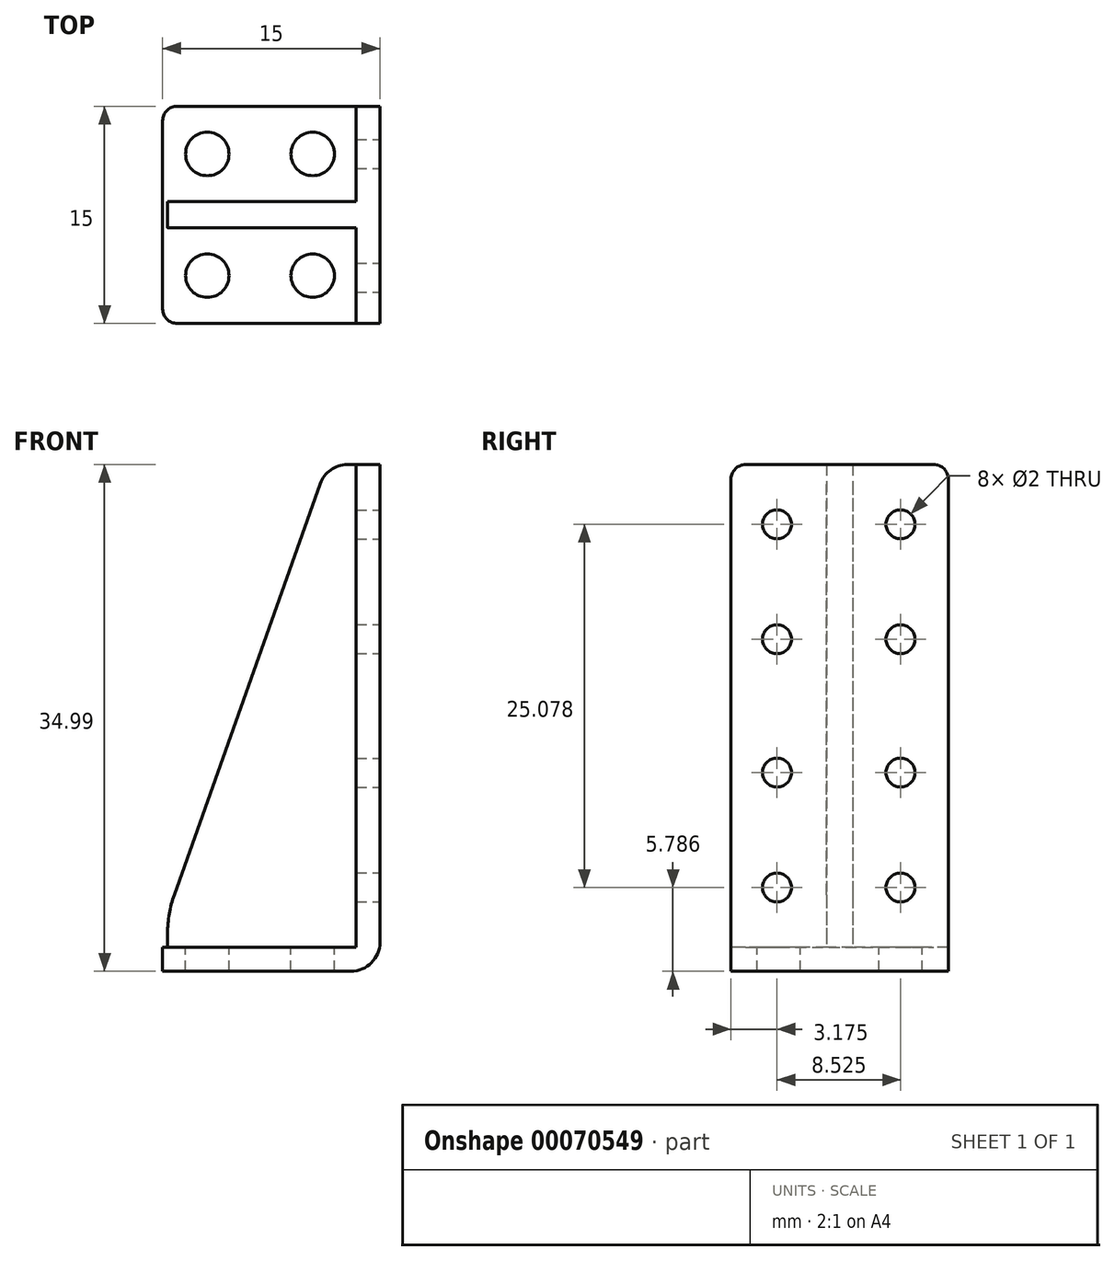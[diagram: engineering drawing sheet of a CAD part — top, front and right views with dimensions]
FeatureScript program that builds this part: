
annotation { "Feature Type Name" : "Feature", "Feature Type Description" : "" }
export const myFeature = defineFeature(function(context is Context, id is Id, definition is map)
    precondition{}
    {
        {
            var Q0;
            Q0=qCreatedBy(makeId("Top.planeOp"),FACE);
            var sketch = newSketch(context, id + "F0", { "sketchPlane" : qUnion([Q0])});
            skLineSegment(sketch, "E0.bottom", {"start": v(0, 0) * mm, "end": v(15, 0) * mm});
            skLineSegment(sketch, "E0.top", {"start": v(0, 15) * mm, "end": v(15, 15) * mm});
            skLineSegment(sketch, "E0.left", {"start": v(0, 0) * mm, "end": v(0, 15) * mm});
            skLineSegment(sketch, "E0.right", {"start": v(15, 0) * mm, "end": v(15, 15) * mm});
            skSolve(sketch);
        }
        {
            var Q0;
            Q0 = qSketchRegion(id + "F0", true);
            extrude(context, id + "F1", {"entities" : qUnion([Q0]), "depth" : 1.66 * mm});
        }
        {
            var Q0;
            Q0=makeQuery(id+"F1.opExtrude","CAP_FACE",FACE,{"disambiguationData":[OSD([sQuery(id+"F0.wireOp",EDGE,"E0.bottom"),sQuery(id+"F0.wireOp",EDGE,"E0.top"),sQuery(id+"F0.wireOp",EDGE,"E0.left"),sQuery(id+"F0.wireOp",EDGE,"E0.right")])],"isStart":false});
            var sketch = newSketch(context, id + "F2", { "sketchPlane" : qUnion([Q0])});
            skLineSegment(sketch, "E1.bottom", {"start": v(15, 15) * mm, "end": v(13.34, 15) * mm});
            skLineSegment(sketch, "E1.top", {"start": v(15, 0) * mm, "end": v(13.34, 0) * mm});
            skLineSegment(sketch, "E1.left", {"start": v(15, 15) * mm, "end": v(15, 0) * mm});
            skLineSegment(sketch, "E1.right", {"start": v(13.34, 15) * mm, "end": v(13.34, 0) * mm});
            skSolve(sketch);
        }
        {
            var Q0;
            Q0 = qSketchRegion(id + "F2", true);
            extrude(context, id + "F3", {"entities" : qUnion([Q0]), "operationType" : NewBodyOperationType.ADD, "depth" : 33.33 * mm});
        }
        {
            var Q0;
            Q0=makeQuery(id+"F3.opExtrude","SWEPT_FACE",FACE,{"disambiguationData":[OSD([sQuery(id+"F2.wireOp",EDGE,"E1.right")])]});
            var sketch = newSketch(context, id + "F4", { "sketchPlane" : qUnion([Q0])});
            skLineSegment(sketch, "E2", {"start": v(-7.5, 35) * mm, "end": v(-7.5, -12.6) * mm, "construction": true});
            skLineSegment(sketch, "E3", {"start": v(-7.5, 35) * mm, "end": v(-6.6, 35) * mm});
            skLineSegment(sketch, "E4", {"start": v(-6.6, 35) * mm, "end": v(-6.6, 1.66) * mm});
            skLineSegment(sketch, "E5", {"start": v(-6.6, 1.66) * mm, "end": v(-7.5, 1.66) * mm});
            skLineSegment(sketch, "E6.MirrorCS", {"start": v(-8.4, 35) * mm, "end": v(-8.4, 1.66) * mm});
            skLineSegment(sketch, "E7.MirrorCS", {"start": v(-8.4, 1.66) * mm, "end": v(-7.5, 1.66) * mm});
            skLineSegment(sketch, "E8.MirrorCS", {"start": v(-7.5, 35) * mm, "end": v(-8.4, 35) * mm});
            skSolve(sketch);
        }
        {
            var Q0;
            Q0 = qSketchRegion(id + "F4", true);
            extrude(context, id + "F5", {"entities" : qUnion([Q0]), "operationType" : NewBodyOperationType.ADD, "depth" : 13 * mm});
        }
        {
            var Q0;
            Q0=makeQuery(id+"F5.opExtrude","CAP_EDGE",EDGE,{"disambiguationData":[OSD([sQuery(id+"F4.wireOp",EDGE,"E3"),sQuery(id+"F4.wireOp",EDGE,"E8.MirrorCS")])],"isStart":false});
            chamfer(context, id + "F6", {"entities" : qUnion([Q0]), "chamferType" : ChamferType.TWO_OFFSETS, "width1" : 11 * mm, "oppositeDirection" : false, "width2" : 31 * mm, "tangentPropagation" : true});
        }
        {
            var Q0;
            Q0=makeQuery(id+"F1.opExtrude","SWEPT_EDGE",EDGE,{"disambiguationData":[OSD([sQuery(id+"F0.wireOp",EDGE,"E0.bottom"),sQuery(id+"F0.wireOp",EDGE,"E0.left")])]});
            var Q1;
            Q1=makeQuery(id+"F1.opExtrude","SWEPT_EDGE",EDGE,{"disambiguationData":[OSD([sQuery(id+"F0.wireOp",EDGE,"E0.top"),sQuery(id+"F0.wireOp",EDGE,"E0.left")])]});
            var Q2;
            {var subQ0=sQuery(id+"F2.wireOp",EDGE,"E1.right");var subQ1=sQuery(id+"F0.wireOp",EDGE,"E0.bottom");Q2=makeQuery(id+"F5.boolean.opBoolean","SPLIT",EDGE,{"disambiguationData":[TD([makeQuery(id+"F1.opExtrude","SWEPT_FACE",FACE,{"disambiguationData":[OSD([subQ1])]})])],"derivedFrom":makeQuery(id+"F3.opExtrude","CAP_EDGE",EDGE,{"disambiguationData":[OSD([subQ0])],"isStart":true})});}
            var Q3;
            {var subQ0=sQuery(id+"F2.wireOp",EDGE,"E1.right");var subQ1=sQuery(id+"F0.wireOp",EDGE,"E0.top");Q3=makeQuery(id+"F5.boolean.opBoolean","SPLIT",EDGE,{"disambiguationData":[TD([makeQuery(id+"F1.opExtrude","SWEPT_FACE",FACE,{"disambiguationData":[OSD([subQ1])]})])],"derivedFrom":makeQuery(id+"F3.opExtrude","CAP_EDGE",EDGE,{"disambiguationData":[OSD([subQ0])],"isStart":true})});}
            var Q4;
            Q4=makeQuery(id+"F3.opExtrude","CAP_EDGE",EDGE,{"disambiguationData":[OSD([sQuery(id+"F2.wireOp",EDGE,"E1.bottom")])],"isStart":false});
            var Q5;
            Q5=makeQuery(id+"F3.opExtrude","CAP_EDGE",EDGE,{"disambiguationData":[OSD([sQuery(id+"F2.wireOp",EDGE,"E1.top")])],"isStart":false});
            fillet(context, id + "F7", {"entities" : qUnion([Q0, Q1, Q2, Q3, Q4, Q5]), "radius" : 1 * mm, "tangentPropagation" : true, "allowEdgeOverflow" : false});
        }
        {
            var Q0;
            {var subQ0=sQuery(id+"F4.wireOp",EDGE,"E8.MirrorCS");var subQ1=sQuery(id+"F4.wireOp",EDGE,"E3");Q0=makeQuery(id+"F6.opChamfer","BLEND_EDGE",EDGE,{"blendedFrom":[makeQuery(id+"F5.opExtrude","CAP_EDGE",EDGE,{"disambiguationData":[OSD([subQ1,subQ0])],"isStart":false}),makeQuery(id+"F5.boolean.opBoolean","MERGE",FACE,{"derivedFrom":[makeQuery(id+"F3.opExtrude","CAP_FACE",FACE,{"disambiguationData":[OSD([sQuery(id+"F2.wireOp",EDGE,"E1.bottom"),sQuery(id+"F2.wireOp",EDGE,"E1.top"),sQuery(id+"F2.wireOp",EDGE,"E1.left"),sQuery(id+"F2.wireOp",EDGE,"E1.right")])],"isStart":false}),makeQuery(id+"F5.opExtrude","SWEPT_FACE",FACE,{"disambiguationData":[OSD([subQ1,subQ0])]})]})],"blendedInto":[makeQuery(id+"F5.boolean.opBoolean","MERGE",FACE,{"derivedFrom":[makeQuery(id+"F3.opExtrude","CAP_FACE",FACE,{"disambiguationData":[OSD([sQuery(id+"F2.wireOp",EDGE,"E1.bottom"),sQuery(id+"F2.wireOp",EDGE,"E1.top"),sQuery(id+"F2.wireOp",EDGE,"E1.left"),sQuery(id+"F2.wireOp",EDGE,"E1.right")])],"isStart":false}),makeQuery(id+"F5.opExtrude","SWEPT_FACE",FACE,{"disambiguationData":[OSD([subQ1,subQ0])]})]})]});}
            var Q1;
            Q1=makeQuery(id+"F1.opExtrude","CAP_EDGE",EDGE,{"disambiguationData":[OSD([sQuery(id+"F0.wireOp",EDGE,"E0.right")])],"isStart":true});
            fillet(context, id + "F8", {"entities" : qUnion([Q0, Q1]), "radius" : 2 * mm, "tangentPropagation" : true, "allowEdgeOverflow" : false});
        }
        {
            var Q0;
            {var subQ0=sQuery(id+"F4.wireOp",EDGE,"E8.MirrorCS");var subQ1=sQuery(id+"F4.wireOp",EDGE,"E3");Q0=makeQuery(id+"F6.opChamfer","BLEND_EDGE",EDGE,{"blendedFrom":[makeQuery(id+"F5.opExtrude","CAP_EDGE",EDGE,{"disambiguationData":[OSD([subQ1,subQ0])],"isStart":false}),makeQuery(id+"F5.opExtrude","CAP_FACE",FACE,{"disambiguationData":[OSD([subQ1,sQuery(id+"F4.wireOp",EDGE,"E4"),sQuery(id+"F4.wireOp",EDGE,"E5"),sQuery(id+"F4.wireOp",EDGE,"E6.MirrorCS"),sQuery(id+"F4.wireOp",EDGE,"E7.MirrorCS"),subQ0])],"isStart":false})],"blendedInto":[makeQuery(id+"F5.opExtrude","CAP_FACE",FACE,{"disambiguationData":[OSD([subQ1,sQuery(id+"F4.wireOp",EDGE,"E4"),sQuery(id+"F4.wireOp",EDGE,"E5"),sQuery(id+"F4.wireOp",EDGE,"E6.MirrorCS"),sQuery(id+"F4.wireOp",EDGE,"E7.MirrorCS"),subQ0])],"isStart":false})]});}
            fillet(context, id + "F9", {"entities" : qUnion([Q0]), "radius" : 8 * mm, "tangentPropagation" : true, "allowEdgeOverflow" : false});
        }
        {
            var Q0;
            Q0=makeQuery(id+"F1.opExtrude","CAP_FACE",FACE,{"disambiguationData":[OSD([sQuery(id+"F0.wireOp",EDGE,"E0.bottom"),sQuery(id+"F0.wireOp",EDGE,"E0.top"),sQuery(id+"F0.wireOp",EDGE,"E0.left"),sQuery(id+"F0.wireOp",EDGE,"E0.right")])],"isStart":false});
            var sketch = newSketch(context, id + "F10", { "sketchPlane" : qUnion([Q0])});
            skLineSegment(sketch, "E9", {"start": v(12.34, 11.7) * mm, "end": v(-2.49, 11.7) * mm, "construction": true});
            skPoint(sketch, "E9.endSnap0", {"position": v(12.34, 11.7) * mm});
            skLineSegment(sketch, "E10", {"start": v(12.34, 3.3) * mm, "end": v(-2.49, 3.3) * mm, "construction": true});
            skLineSegment(sketch, "E11", {"start": v(0.34, 7.5) * mm, "end": v(14.3, 7.5) * mm, "construction": true});
            skLineSegment(sketch, "E12", {"start": v(14.3, 7.5) * mm, "end": v(-2.6, 7.5) * mm, "construction": true});
            skCircle(sketch, "E13", {"center": v(3.08, 11.7) * mm, "radius": 1.5 * mm});
            skCircle(sketch, "E14", {"center": v(10.36, 11.7) * mm, "radius": 1.5 * mm});
            skCircle(sketch, "E15.MirrorC", {"center": v(3.08, 3.3) * mm, "radius": 1.5 * mm});
            skCircle(sketch, "E16.MirrorC", {"center": v(10.36, 3.3) * mm, "radius": 1.5 * mm});
            skSolve(sketch);
        }
        {
            var Q0;
            Q0 = qSketchRegion(id + "F10", true);
            extrude(context, id + "F11", {"entities" : qUnion([Q0]), "operationType" : NewBodyOperationType.REMOVE, "oppositeDirection" : true, "depth" : 25 * mm});
        }
        {
            var Q0;
            {var subQ0=sQuery(id+"F2.wireOp",EDGE,"E1.right");var subQ2=sQuery(id+"F0.wireOp",EDGE,"E0.top");Q0=makeQuery(id+"F5.boolean.opBoolean","SPLIT",FACE,{"disambiguationData":[TD([makeQuery(id+"F1.opExtrude","SWEPT_FACE",FACE,{"disambiguationData":[OSD([subQ2])]})])],"derivedFrom":makeQuery(id+"F3.opExtrude","SWEPT_FACE",FACE,{"disambiguationData":[OSD([subQ0])]})});}
            var sketch = newSketch(context, id + "F12", { "sketchPlane" : qUnion([Q0])});
            skLineSegment(sketch, "E17", {"start": v(-7.44, -1.29) * mm, "end": v(-7.44, 35.8) * mm, "construction": true});
            skLineSegment(sketch, "E18", {"start": v(-11.7, 2.66) * mm, "end": v(-11.7, 35.8) * mm, "construction": true});
            skLineSegment(sketch, "E19", {"start": v(-15, 18.32) * mm, "end": v(1.6, 18.32) * mm, "construction": true});
            skLineSegment(sketch, "E20", {"start": v(-20.6, 35) * mm, "end": v(1.6, 35) * mm, "construction": true});
            skLineSegment(sketch, "E21", {"start": v(-21.36, 2.66) * mm, "end": v(1.6, 2.66) * mm, "construction": true});
            skCircle(sketch, "E22", {"center": v(-11.7, 22.93) * mm, "radius": 1 * mm});
            skCircle(sketch, "E23", {"center": v(-11.7, 30.86) * mm, "radius": 1 * mm});
            skCircle(sketch, "E24.MirrorC", {"center": v(-11.7, 13.72) * mm, "radius": 1 * mm});
            skCircle(sketch, "E25.MirrorC", {"center": v(-11.7, 5.79) * mm, "radius": 1 * mm});
            skCircle(sketch, "E26.MirrorC", {"center": v(-3.18, 30.86) * mm, "radius": 1 * mm});
            skCircle(sketch, "E27.MirrorC", {"center": v(-3.18, 22.93) * mm, "radius": 1 * mm});
            skCircle(sketch, "E28.MirrorC", {"center": v(-3.18, 13.72) * mm, "radius": 1 * mm});
            skCircle(sketch, "E29.MirrorC", {"center": v(-3.18, 5.79) * mm, "radius": 1 * mm});
            skSolve(sketch);
        }
        {
            var Q0;
            Q0 = qSketchRegion(id + "F12", true);
            extrude(context, id + "F13", {"entities" : qUnion([Q0]), "operationType" : NewBodyOperationType.REMOVE, "depth" : 25 * mm, "hasSecondDirection" : true, "secondDirectionOppositeDirection" : true, "secondDirectionDepth" : 25 * mm});
        }
    });
